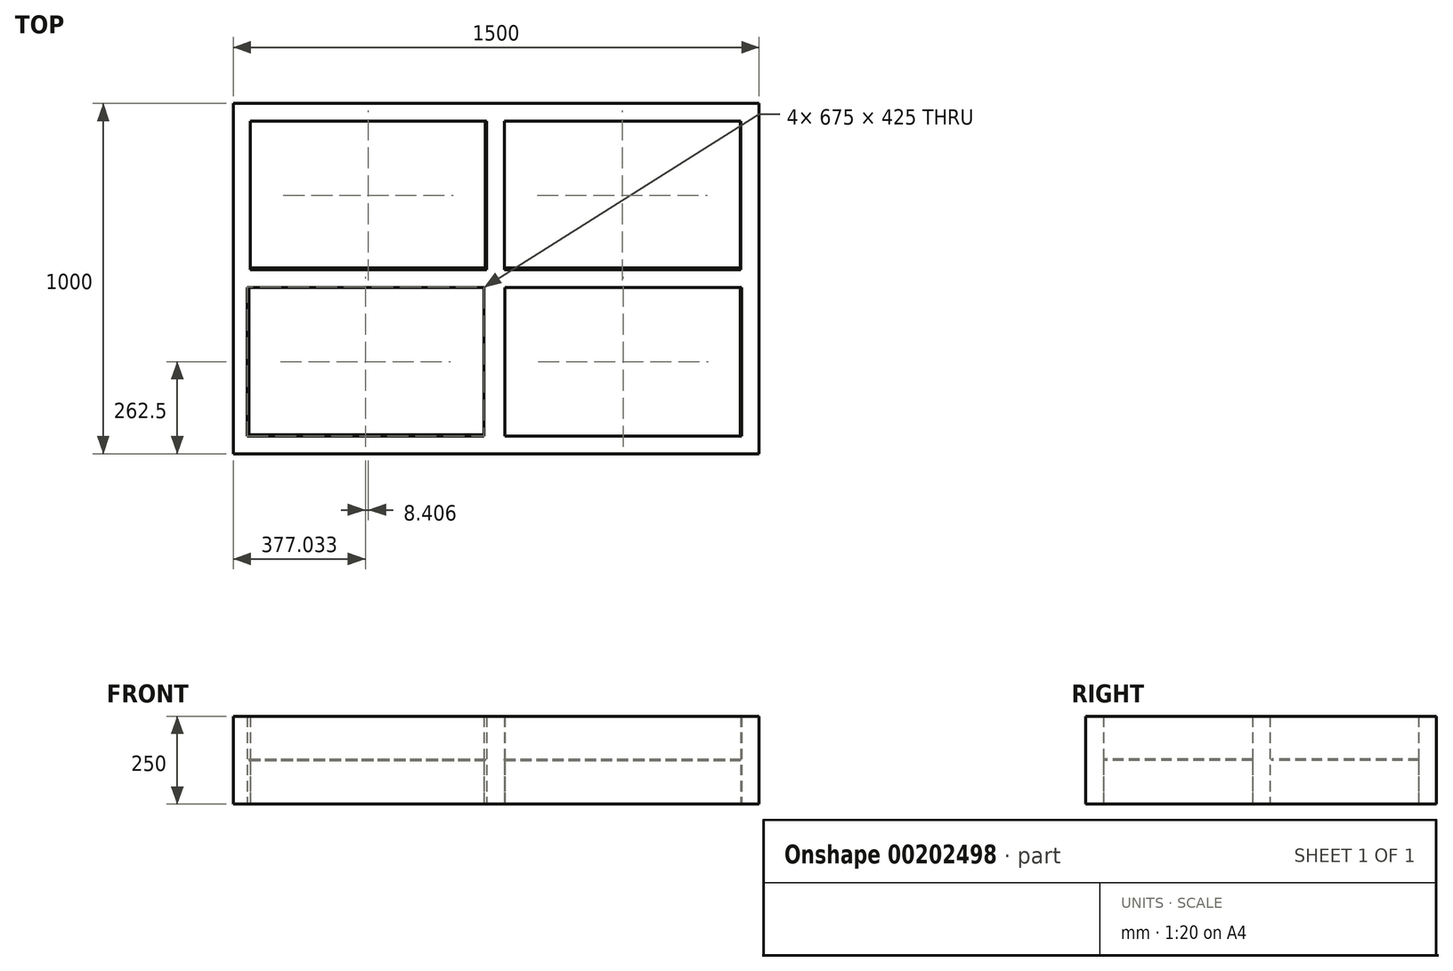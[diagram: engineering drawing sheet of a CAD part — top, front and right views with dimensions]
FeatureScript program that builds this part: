
annotation { "Feature Type Name" : "Feature", "Feature Type Description" : "" }
export const myFeature = defineFeature(function(context is Context, id is Id, definition is map)
    precondition{}
    {
        {
            var Q0;
            Q0=qCreatedBy(makeId("Top.planeOp"),FACE);
            var sketch = newSketch(context, id + "F0", { "sketchPlane" : qUnion([Q0])});
            skLineSegment(sketch, "E0.bottom", {"start": v(750, 500) * mm, "end": v(-750, 500) * mm});
            skLineSegment(sketch, "E0.top", {"start": v(750, -500) * mm, "end": v(-750, -500) * mm});
            skLineSegment(sketch, "E0.left", {"start": v(750, 500) * mm, "end": v(750, -500) * mm});
            skLineSegment(sketch, "E0.right", {"start": v(-750, 500) * mm, "end": v(-750, -500) * mm});
            skPoint(sketch, "E0.middle", {"position": v(0, 0) * mm});
            skLineSegment(sketch, "E1.bottom", {"start": v(-702.06, 450) * mm, "end": v(-27.06, 450) * mm});
            skLineSegment(sketch, "E1.top", {"start": v(-702.06, 25) * mm, "end": v(-27.06, 25) * mm});
            skLineSegment(sketch, "E1.left", {"start": v(-702.06, 450) * mm, "end": v(-702.06, 25) * mm});
            skLineSegment(sketch, "E1.right", {"start": v(-27.06, 450) * mm, "end": v(-27.06, 25) * mm});
            skLineSegment(sketch, "E2.bottom", {"start": v(-710.47, -25) * mm, "end": v(-35.47, -25) * mm});
            skLineSegment(sketch, "E2.top", {"start": v(-710.47, -450) * mm, "end": v(-35.47, -450) * mm});
            skLineSegment(sketch, "E2.left", {"start": v(-710.47, -25) * mm, "end": v(-710.47, -450) * mm});
            skLineSegment(sketch, "E2.right", {"start": v(-35.47, -25) * mm, "end": v(-35.47, -450) * mm});
            skLineSegment(sketch, "E3.bottom", {"start": v(22.94, 450) * mm, "end": v(697.94, 450) * mm});
            skLineSegment(sketch, "E3.top", {"start": v(22.94, 25) * mm, "end": v(697.94, 25) * mm});
            skLineSegment(sketch, "E3.left", {"start": v(22.94, 450) * mm, "end": v(22.94, 25) * mm});
            skLineSegment(sketch, "E3.right", {"start": v(697.94, 450) * mm, "end": v(697.94, 25) * mm});
            skLineSegment(sketch, "E4.bottom", {"start": v(25, -25) * mm, "end": v(700, -25) * mm});
            skLineSegment(sketch, "E4.top", {"start": v(25, -450) * mm, "end": v(700, -450) * mm});
            skLineSegment(sketch, "E4.left", {"start": v(25, -25) * mm, "end": v(25, -450) * mm});
            skLineSegment(sketch, "E4.right", {"start": v(700, -25) * mm, "end": v(700, -450) * mm});
            skSolve(sketch);
        }
        {
            var Q0;
            Q0=makeQuery(id+"F0.imprint","IMPRINT",FACE,{"disambiguationData":[TD([[makeQuery(id+"F0.imprint","IMPRINT",EDGE,{"derivedFrom":sQuery(id+"F0.wireOp",EDGE,"E0.bottom")}),1.0]])]});
            extrude(context, id + "F1", {"entities" : qUnion([Q0]), "endBound" : BoundingType.SYMMETRIC, "depth" : 250 * mm});
        }
        {
            var Q0;
            Q0=qCreatedBy(makeId("Top.planeOp"),FACE);
            var sketch = newSketch(context, id + "F2", { "sketchPlane" : qUnion([Q0])});
            skLineSegment(sketch, "E5.bottom", {"start": v(-705.87, 455.16) * mm, "end": v(-30.87, 455.16) * mm});
            skLineSegment(sketch, "E5.top", {"start": v(-705.87, 30.16) * mm, "end": v(-30.87, 30.16) * mm});
            skLineSegment(sketch, "E5.left", {"start": v(-705.87, 455.16) * mm, "end": v(-705.87, 30.16) * mm});
            skLineSegment(sketch, "E5.right", {"start": v(-30.87, 455.16) * mm, "end": v(-30.87, 30.16) * mm});
            skLineSegment(sketch, "E6.bottom", {"start": v(-705.87, -20.65) * mm, "end": v(-30.87, -20.65) * mm});
            skLineSegment(sketch, "E6.top", {"start": v(-705.87, -445.65) * mm, "end": v(-30.87, -445.65) * mm});
            skLineSegment(sketch, "E6.left", {"start": v(-705.87, -20.65) * mm, "end": v(-705.87, -445.65) * mm});
            skLineSegment(sketch, "E6.right", {"start": v(-30.87, -20.65) * mm, "end": v(-30.87, -445.65) * mm});
            skLineSegment(sketch, "E7.bottom", {"start": v(22, 455.16) * mm, "end": v(697, 455.16) * mm});
            skLineSegment(sketch, "E7.top", {"start": v(22, 30.16) * mm, "end": v(697, 30.16) * mm});
            skLineSegment(sketch, "E7.left", {"start": v(22, 455.16) * mm, "end": v(22, 30.16) * mm});
            skLineSegment(sketch, "E7.right", {"start": v(697, 455.16) * mm, "end": v(697, 30.16) * mm});
            skLineSegment(sketch, "E8.bottom", {"start": v(22, -25.25) * mm, "end": v(697, -25.25) * mm});
            skLineSegment(sketch, "E8.top", {"start": v(22, -450.25) * mm, "end": v(697, -450.25) * mm});
            skLineSegment(sketch, "E8.left", {"start": v(22, -25.25) * mm, "end": v(22, -450.25) * mm});
            skLineSegment(sketch, "E8.right", {"start": v(697, -25.25) * mm, "end": v(697, -450.25) * mm});
            skSolve(sketch);
        }
        {
            var Q0;
            Q0=qSketchRegion(id+"F2",true);
            extrude(context, id + "F3", {"entities" : qUnion([Q0]), "operationType" : NewBodyOperationType.ADD, "depth" : 3 * mm});
        }
    });
